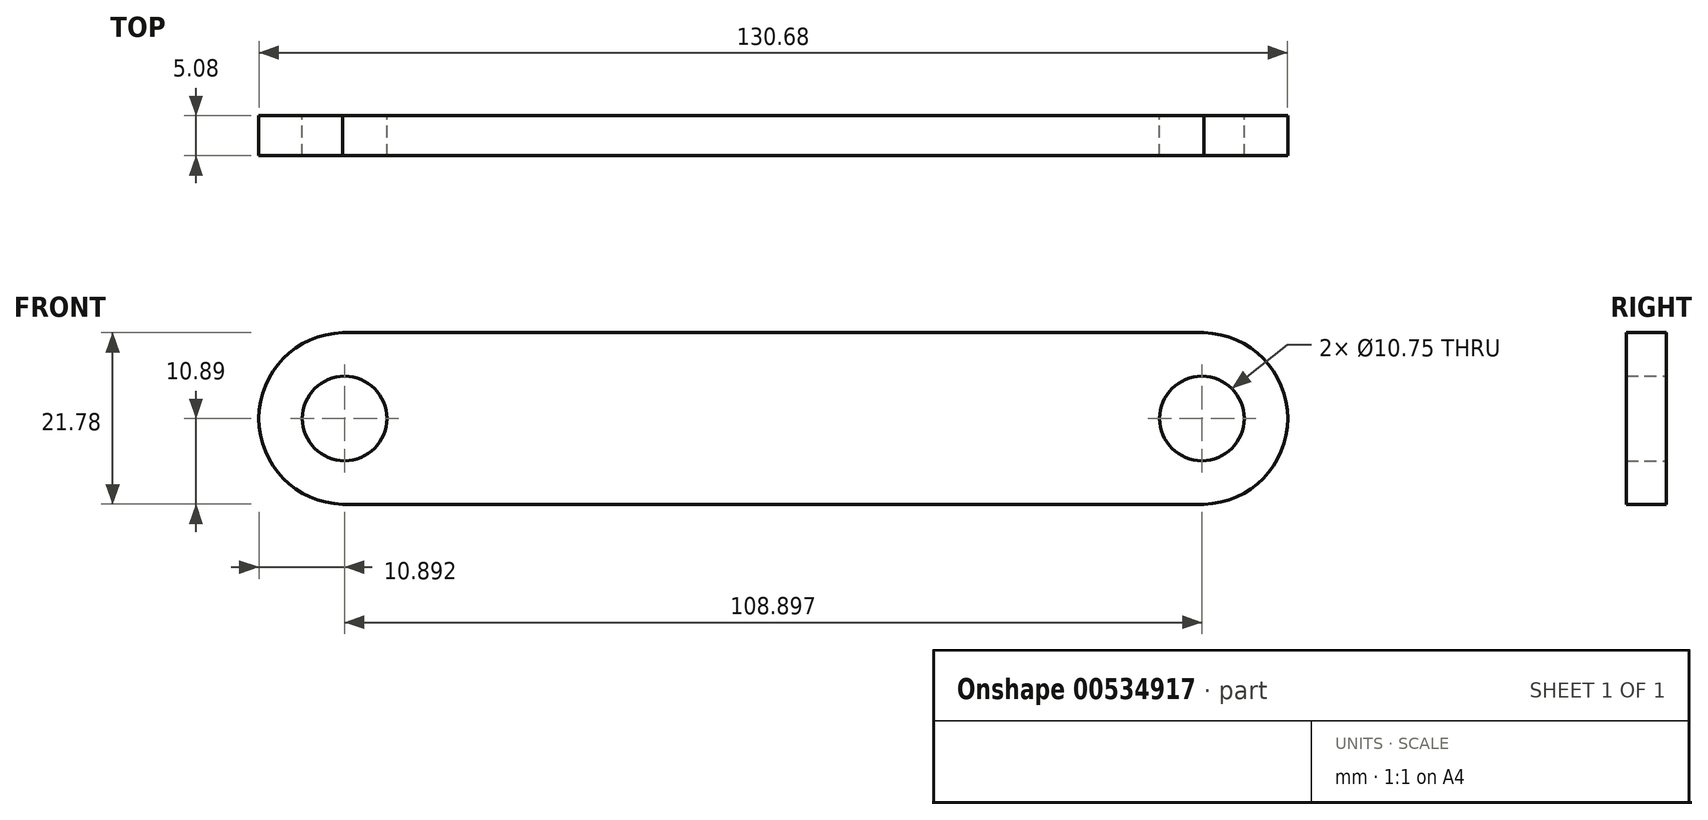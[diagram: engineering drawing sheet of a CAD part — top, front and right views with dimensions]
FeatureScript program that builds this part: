
annotation { "Feature Type Name" : "Feature", "Feature Type Description" : "" }
export const myFeature = defineFeature(function(context is Context, id is Id, definition is map)
    precondition{}
    {
        {
            var Q0;
            Q0=qCreatedBy(makeId("Front.planeOp"),FACE);
            var sketch = newSketch(context, id + "F0", { "sketchPlane" : qUnion([Q0])});
            skArc(sketch, "E0", {"start": v(-54.68, 10.9) * mm, "mid": v(-65.34, 0) * mm, "end": v(-54.68, -10.9) * mm});
            skLineSegment(sketch, "E1", {"start": v(-104.36, 0) * mm, "end": v(104.44, 0) * mm, "construction": true});
            skLineSegment(sketch, "E2", {"start": v(0, 69.15) * mm, "end": v(0, -67.29) * mm, "construction": true});
            skArc(sketch, "E3.MirrorCS", {"start": v(54.68, 10.9) * mm, "mid": v(65.34, 0) * mm, "end": v(54.68, -10.9) * mm});
            skLineSegment(sketch, "E4", {"start": v(-54.68, 10.9) * mm, "end": v(54.68, 10.9) * mm});
            skLineSegment(sketch, "E5", {"start": v(-54.68, -10.9) * mm, "end": v(54.68, -10.9) * mm});
            skCircle(sketch, "E6", {"center": v(-54.45, 0) * mm, "radius": 5.37 * mm});
            skCircle(sketch, "E7.MirrorC", {"center": v(54.45, 0) * mm, "radius": 5.37 * mm});
            skSolve(sketch);
        }
        {
            var Q0;
            Q0=makeQuery(id+"F0.imprint","IMPRINT",FACE,{"disambiguationData":[TD([[makeQuery(id+"F0.imprint","IMPRINT",EDGE,{"derivedFrom":sQuery(id+"F0.wireOp",EDGE,"E0")}),1.0]])]});
            extrude(context, id + "F1", {"entities" : qUnion([Q0]), "depth" : 5.08 * mm, "offsetDistance" : 25.4 * mm});
        }
    });
